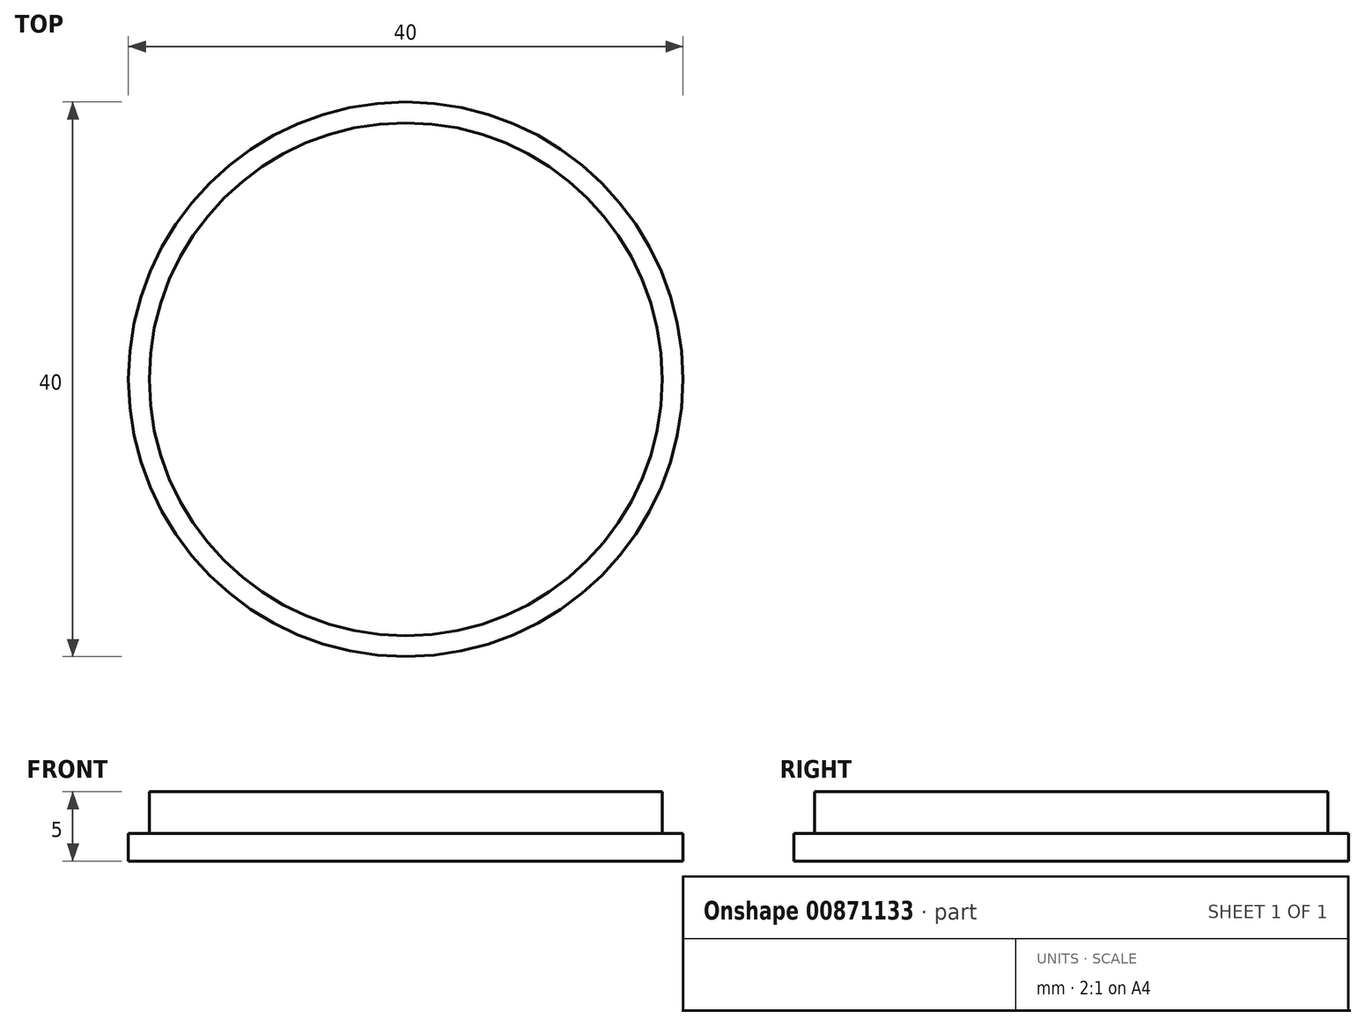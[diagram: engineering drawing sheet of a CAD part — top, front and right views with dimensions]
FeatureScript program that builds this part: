
annotation { "Feature Type Name" : "Feature", "Feature Type Description" : "" }
export const myFeature = defineFeature(function(context is Context, id is Id, definition is map)
    precondition{}
    {
        {
            var Q0;
            Q0=qCreatedBy(makeId("Top.planeOp"),FACE);
            var sketch = newSketch(context, id + "F0", { "sketchPlane" : qUnion([Q0])});
            skCircle(sketch, "E0", {"center": v(0, 0) * mm, "radius": 20 * mm});
            skCircle(sketch, "E1", {"center": v(0, 0) * mm, "radius": 18.5 * mm});
            skSolve(sketch);
        }
        {
            var Q0;
            Q0=makeQuery(id+"F0.imprint","IMPRINT",FACE,{"disambiguationData":[TD([[makeQuery(id+"F0.imprint","IMPRINT",EDGE,{"derivedFrom":sQuery(id+"F0.wireOp",EDGE,"E0")}),1.0]])]});
            var Q1;
            Q1=sQuery(id+"F0.wireOp",EDGE,"E0");
            extrude(context, id + "F1", {"entities" : qUnion([Q0]), "surfaceEntities" : qUnion([Q1]), "depth" : 2 * mm, "offsetDistance" : 25 * mm});
        }
        {
            var Q0;
            Q0=makeQuery(id+"F0.imprint","IMPRINT",FACE,{"disambiguationData":[TD([[makeQuery(id+"F0.imprint","IMPRINT",EDGE,{"derivedFrom":sQuery(id+"F0.wireOp",EDGE,"E1")}),1.0]])]});
            var Q1;
            Q1=sQuery(id+"F0.wireOp",EDGE,"E0");
            extrude(context, id + "F2", {"entities" : qUnion([Q0]), "operationType" : NewBodyOperationType.ADD, "surfaceOperationType" : NewSurfaceOperationType.ADD, "surfaceEntities" : qUnion([Q1]), "depth" : 5 * mm, "offsetDistance" : 25 * mm});
        }
    });
